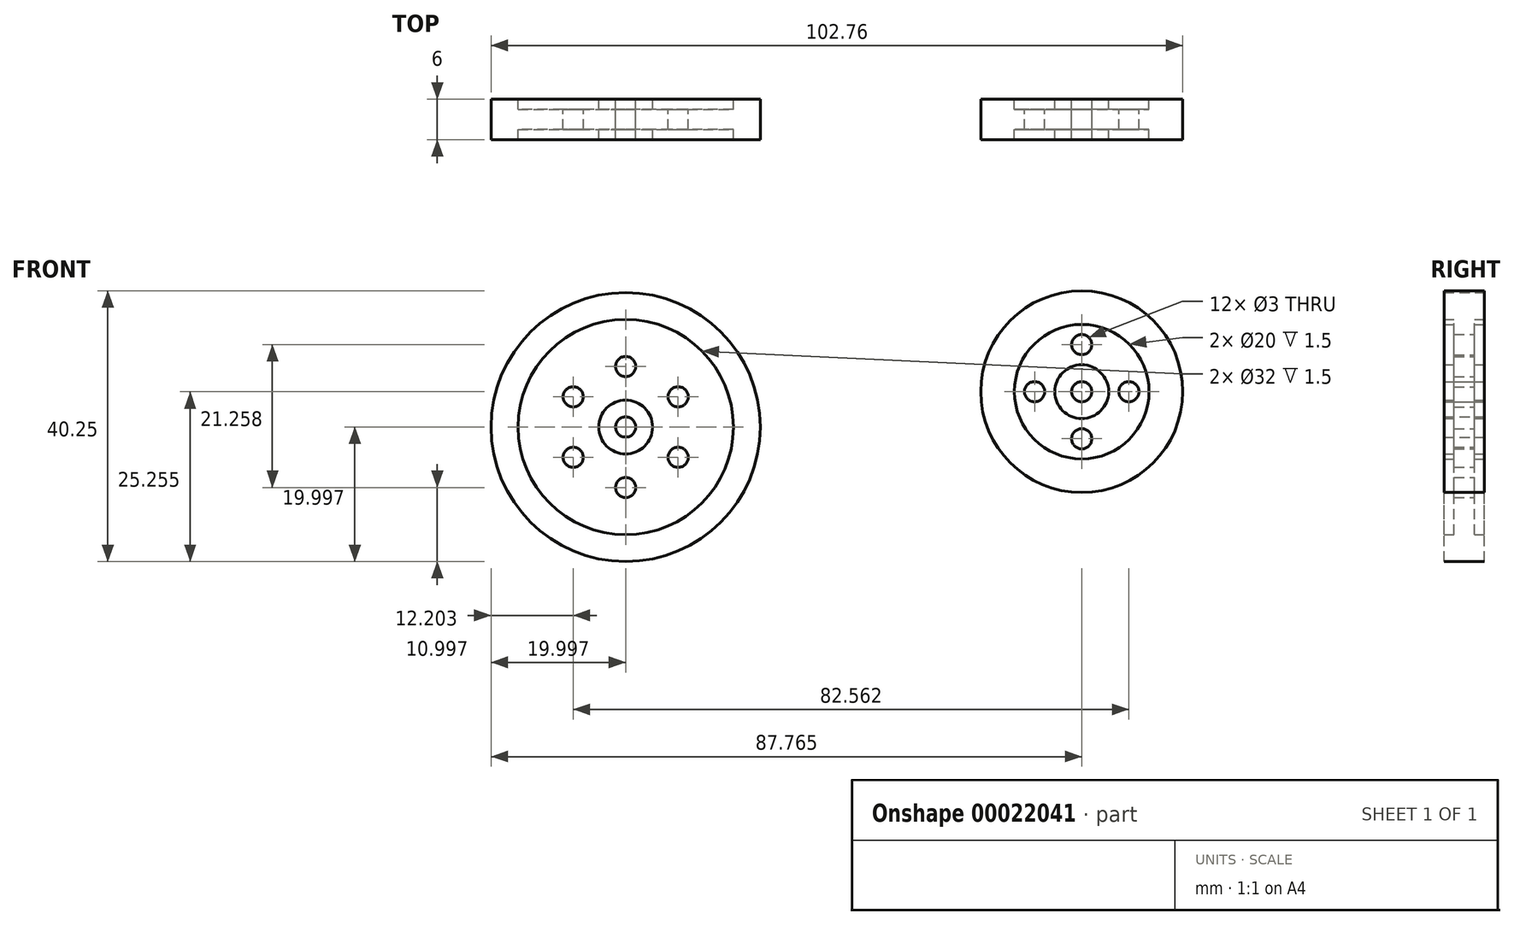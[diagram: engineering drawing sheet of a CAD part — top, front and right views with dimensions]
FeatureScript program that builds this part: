
annotation { "Feature Type Name" : "Feature", "Feature Type Description" : "" }
export const myFeature = defineFeature(function(context is Context, id is Id, definition is map)
    precondition{}
    {
        {
            var Q0;
            Q0=qCreatedBy(makeId("Front.planeOp"),FACE);
            var sketch = newSketch(context, id + "F0", { "sketchPlane" : qUnion([Q0])});
            skCircle(sketch, "E0", {"center": v(-44.2, 7.6) * mm, "radius": 20 * mm});
            skCircle(sketch, "E1", {"center": v(-44.2, 16.6) * mm, "radius": 1.5 * mm});
            skPoint(sketch, "E2", {"position": v(-44.2, 27.6) * mm});
            skCircle(sketch, "E3.1.0", {"center": v(-52, 12.1) * mm, "radius": 1.5 * mm});
            skCircle(sketch, "E3.2.0", {"center": v(-52, 3.1) * mm, "radius": 1.5 * mm});
            skCircle(sketch, "E3.3.0", {"center": v(-44.2, -1.4) * mm, "radius": 1.5 * mm});
            skCircle(sketch, "E3.4.0", {"center": v(-36.4, 3.1) * mm, "radius": 1.5 * mm});
            skCircle(sketch, "E3.5.0", {"center": v(-36.4, 12.1) * mm, "radius": 1.5 * mm});
            skCircle(sketch, "E4", {"center": v(-44.2, 7.6) * mm, "radius": 16 * mm});
            skCircle(sketch, "E5", {"center": v(-44.2, 7.6) * mm, "radius": 4 * mm});
            skLineSegment(sketch, "E6.trimOffspring", {"start": v(-44.2, 15.1) * mm, "end": v(-44.2, 18.1) * mm});
            skCircle(sketch, "E7", {"center": v(-44.2, 7.6) * mm, "radius": 1.5 * mm});
            skSolve(sketch);
        }
        {
            var Q0;
            Q0=makeQuery(id+"F0.imprint","IMPRINT",FACE,{"disambiguationData":[TD([[makeQuery(id+"F0.imprint","IMPRINT",EDGE,{"derivedFrom":sQuery(id+"F0.wireOp",EDGE,"E0")}),1.0]])]});
            extrude(context, id + "F1", {"entities" : qUnion([Q0]), "endBound" : BoundingType.SYMMETRIC, "depth" : 6 * mm});
        }
        {
            var Q0;
            Q0=makeQuery(id+"F0.imprint","IMPRINT",FACE,{"disambiguationData":[TD([[makeQuery(id+"F0.imprint","IMPRINT",EDGE,{"derivedFrom":sQuery(id+"F0.wireOp",EDGE,"E3.1.0")}),-1.0]])]});
            extrude(context, id + "F2", {"entities" : qUnion([Q0]), "operationType" : NewBodyOperationType.ADD, "endBound" : BoundingType.SYMMETRIC, "depth" : 3 * mm});
        }
        {
            var Q0;
            Q0=makeQuery(id+"F0.imprint","IMPRINT",FACE,{"disambiguationData":[TD([[makeQuery(id+"F0.imprint","IMPRINT",EDGE,{"derivedFrom":sQuery(id+"F0.wireOp",EDGE,"E5")}),1.0]])]});
            extrude(context, id + "F3", {"entities" : qUnion([Q0]), "operationType" : NewBodyOperationType.ADD, "endBound" : BoundingType.SYMMETRIC, "depth" : 6 * mm});
        }
        {
            var Q0;
            Q0=sQuery(id+"F0.wireOp",VERTEX,"E0.center");
            var Q1;
            Q1=makeQuery(id+"F1.opExtrude","SWEPT_BODY",BODY,{"disambiguationData":[OSD([sQuery(id+"F0.wireOp",EDGE,"E0"),sQuery(id+"F0.wireOp",EDGE,"E4")])]});
            hole(context, id + "F4", {"style" : HoleStyle.SIMPLE, "holeDiameter" : 3 * mm, "endStyle" : HoleEndStyle.THROUGH, "locations" : qUnion([Q0]), "scope" : qUnion([Q1])});
        }
        {
            var Q0;
            Q0=qCreatedBy(makeId("Front.planeOp"),FACE);
            var sketch = newSketch(context, id + "F5", { "sketchPlane" : qUnion([Q0])});
            skCircle(sketch, "E8", {"center": v(23.56, 12.86) * mm, "radius": 15 * mm});
            skCircle(sketch, "E9", {"center": v(23.56, 12.86) * mm, "radius": 10 * mm});
            skPoint(sketch, "E10", {"position": v(23.56, 19.86) * mm});
            skCircle(sketch, "E11", {"center": v(23.56, 19.86) * mm, "radius": 1.5 * mm});
            skCircle(sketch, "E12.1.0", {"center": v(16.56, 12.86) * mm, "radius": 1.5 * mm});
            skCircle(sketch, "E12.2.0", {"center": v(23.56, 5.86) * mm, "radius": 1.5 * mm});
            skCircle(sketch, "E12.3.0", {"center": v(30.56, 12.86) * mm, "radius": 1.5 * mm});
            skCircle(sketch, "E13", {"center": v(23.56, 12.86) * mm, "radius": 4 * mm});
            skCircle(sketch, "E14", {"center": v(23.56, 12.86) * mm, "radius": 1.5 * mm});
            skSolve(sketch);
        }
        {
            var Q0;
            Q0=makeQuery(id+"F5.imprint","IMPRINT",FACE,{"disambiguationData":[TD([[makeQuery(id+"F5.imprint","IMPRINT",EDGE,{"derivedFrom":sQuery(id+"F5.wireOp",EDGE,"E13")}),1.0]])]});
            extrude(context, id + "F6", {"entities" : qUnion([Q0]), "endBound" : BoundingType.SYMMETRIC, "depth" : 6 * mm});
        }
        {
            var Q0;
            Q0=makeQuery(id+"F5.imprint","IMPRINT",FACE,{"disambiguationData":[TD([[makeQuery(id+"F5.imprint","IMPRINT",EDGE,{"derivedFrom":sQuery(id+"F5.wireOp",EDGE,"E9")}),1.0]])]});
            extrude(context, id + "F7", {"entities" : qUnion([Q0]), "operationType" : NewBodyOperationType.ADD, "endBound" : BoundingType.SYMMETRIC, "depth" : 3 * mm});
        }
        {
            var Q0;
            Q0=makeQuery(id+"F5.imprint","IMPRINT",FACE,{"disambiguationData":[TD([[makeQuery(id+"F5.imprint","IMPRINT",EDGE,{"derivedFrom":sQuery(id+"F5.wireOp",EDGE,"E8")}),1.0]])]});
            extrude(context, id + "F8", {"entities" : qUnion([Q0]), "operationType" : NewBodyOperationType.ADD, "endBound" : BoundingType.SYMMETRIC, "depth" : 6 * mm});
        }
    });
